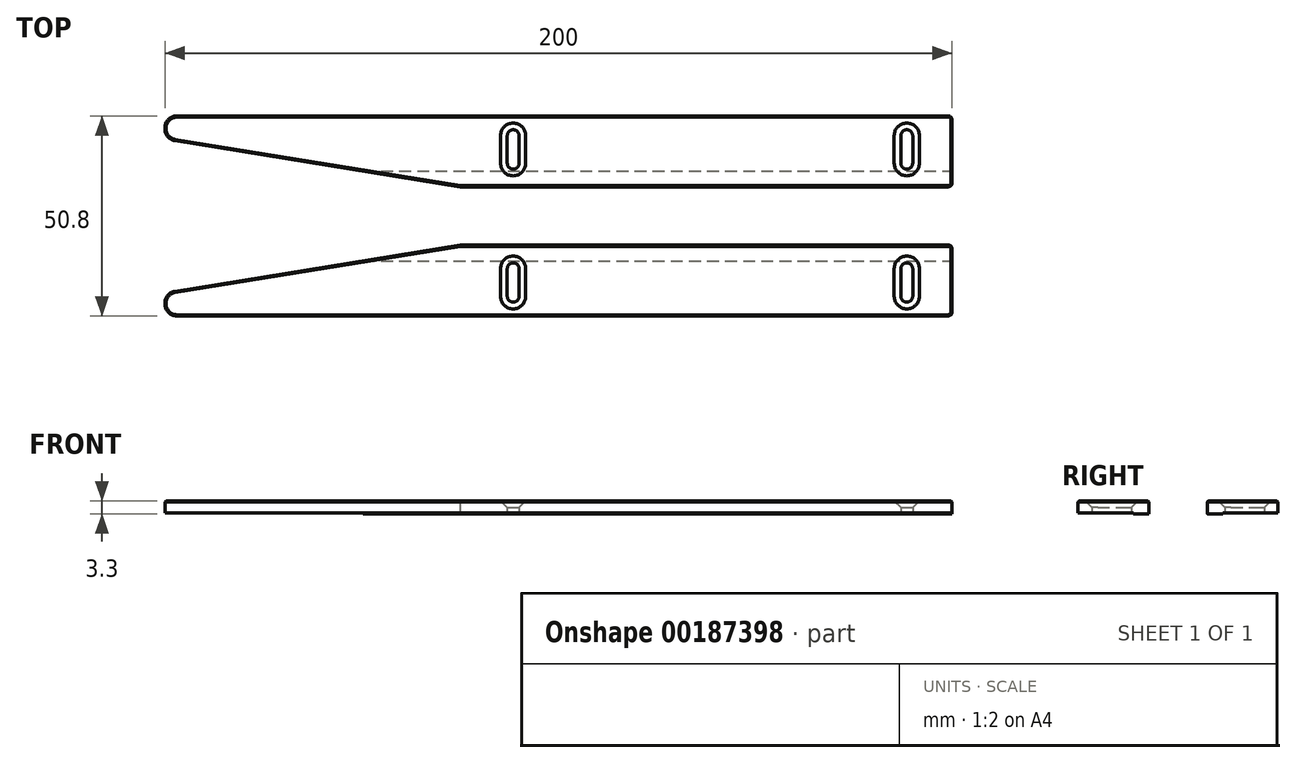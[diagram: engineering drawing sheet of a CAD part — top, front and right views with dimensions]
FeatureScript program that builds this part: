
annotation { "Feature Type Name" : "Feature", "Feature Type Description" : "" }
export const myFeature = defineFeature(function(context is Context, id is Id, definition is map)
    precondition{}
    {
        {
            var Q0;
            Q0=qCreatedBy(makeId("Top.planeOp"),FACE);
            var sketch = newSketch(context, id + "F0", { "sketchPlane" : qUnion([Q0])});
            skLineSegment(sketch, "E0.bottom", {"start": v(0, 0) * mm, "end": v(200, 0) * mm});
            skLineSegment(sketch, "E0.top", {"start": v(0, 18) * mm, "end": v(200, 18) * mm});
            skLineSegment(sketch, "E0.left", {"start": v(0, 0) * mm, "end": v(0, 18) * mm});
            skLineSegment(sketch, "E0.right", {"start": v(200, 0) * mm, "end": v(200, 18) * mm});
            skLineSegment(sketch, "E1.bottom", {"start": v(89.97, 5) * mm, "end": v(86.97, 5) * mm});
            skLineSegment(sketch, "E1.top", {"start": v(89.97, 12) * mm, "end": v(86.97, 12) * mm});
            skLineSegment(sketch, "E1.left", {"start": v(89.97, 5) * mm, "end": v(89.97, 12) * mm});
            skLineSegment(sketch, "E1.right", {"start": v(86.97, 5) * mm, "end": v(86.97, 12) * mm});
            skPoint(sketch, "E1.middle", {"position": v(88.47, 8.5) * mm});
            skLineSegment(sketch, "E2.bottom", {"start": v(189.97, 5) * mm, "end": v(186.97, 5) * mm});
            skLineSegment(sketch, "E2.top", {"start": v(189.97, 12) * mm, "end": v(186.97, 12) * mm});
            skLineSegment(sketch, "E2.left", {"start": v(189.97, 5) * mm, "end": v(189.97, 12) * mm});
            skLineSegment(sketch, "E2.right", {"start": v(186.97, 5) * mm, "end": v(186.97, 12) * mm});
            skPoint(sketch, "E2.middle", {"position": v(188.47, 8.5) * mm});
            skArc(sketch, "E3", {"start": v(86.97, 12) * mm, "mid": v(88.47, 13.5) * mm, "end": v(89.97, 12) * mm});
            skArc(sketch, "E4", {"start": v(186.97, 12) * mm, "mid": v(188.47, 13.5) * mm, "end": v(189.97, 12) * mm});
            skArc(sketch, "E5", {"start": v(86.97, 5) * mm, "mid": v(88.47, 3.5) * mm, "end": v(89.97, 5) * mm});
            skArc(sketch, "E6", {"start": v(186.97, 5) * mm, "mid": v(188.47, 3.5) * mm, "end": v(189.97, 5) * mm});
            skLineSegment(sketch, "E7", {"start": v(0, 5.85) * mm, "end": v(75.04, 18) * mm});
            skSolve(sketch);
        }
        {
            var Q0;
            {var subQ0=sQuery(id+"F0.wireOp",EDGE,"E0.bottom");Q0=makeQuery(id+"F0.imprint","IMPRINT",FACE,{"disambiguationData":[TD([[makeQuery(id+"F0.imprint","IMPRINT",EDGE,{"derivedFrom":subQ0}),1.0]])]});}
            extrude(context, id + "F1", {"entities" : qUnion([Q0]), "depth" : 3 * mm});
        }
        {
            var Q0;
            Q0=makeQuery(id+"F1.opExtrude","CAP_FACE",FACE,{"disambiguationData":[OSD([sQuery(id+"F0.wireOp",EDGE,"E0.bottom"),sQuery(id+"F0.wireOp",EDGE,"E0.top"),sQuery(id+"F0.wireOp",EDGE,"E0.left"),sQuery(id+"F0.wireOp",EDGE,"E0.right"),sQuery(id+"F0.wireOp",EDGE,"E1.left"),sQuery(id+"F0.wireOp",EDGE,"E1.right"),sQuery(id+"F0.wireOp",EDGE,"E2.left"),sQuery(id+"F0.wireOp",EDGE,"E2.right"),sQuery(id+"F0.wireOp",EDGE,"E3"),sQuery(id+"F0.wireOp",EDGE,"E4"),sQuery(id+"F0.wireOp",EDGE,"E5"),sQuery(id+"F0.wireOp",EDGE,"E6"),sQuery(id+"F0.wireOp",EDGE,"E7")])],"isStart":true});
            var sketch = newSketch(context, id + "F2", { "sketchPlane" : qUnion([Q0])});
            skLineSegment(sketch, "E8", {"start": v(75.04, -18) * mm, "end": v(50.33, -14) * mm});
            skLineSegment(sketch, "E9", {"start": v(50.33, -14) * mm, "end": v(200, -14) * mm});
            skLineSegment(sketch, "E10", {"start": v(200, -14) * mm, "end": v(200, -18) * mm});
            skLineSegment(sketch, "E11", {"start": v(200, -18) * mm, "end": v(75.04, -18) * mm});
            skSolve(sketch);
        }
        {
            var Q0;
            {var subQ6=sQuery(id+"F2.wireOp",EDGE,"E8");Q0=makeQuery(id+"F2.imprint","IMPRINT",FACE,{"disambiguationData":[TD([[makeQuery(id+"F2.imprint","IMPRINT",EDGE,{"derivedFrom":subQ6}),1.0]])]});}
            extrude(context, id + "F3", {"entities" : qUnion([Q0]), "operationType" : NewBodyOperationType.ADD, "depth" : .3 * mm});
        }
        {
            var Q0;
            Q0=makeQuery(id+"F1.opExtrude","SWEPT_FACE",FACE,{"disambiguationData":[OSD([sQuery(id+"F0.wireOp",EDGE,"E0.bottom")])]});
            cPlane(context, id + "F4", {"entities" : qUnion([Q0]), "cplaneType" : CPlaneType.OFFSET, "offset" : 25.4 * mm, "oppositeDirection" : true, "width" : 152.4 * mm, "height" : 152.4 * mm});
        }
        {
            var Q0;
            Q0=makeQuery(id+"F1.opExtrude","SWEPT_BODY",BODY,{"disambiguationData":[OSD([sQuery(id+"F0.wireOp",EDGE,"E0.bottom"),sQuery(id+"F0.wireOp",EDGE,"E0.top"),sQuery(id+"F0.wireOp",EDGE,"E0.left"),sQuery(id+"F0.wireOp",EDGE,"E0.right"),sQuery(id+"F0.wireOp",EDGE,"E1.left"),sQuery(id+"F0.wireOp",EDGE,"E1.right"),sQuery(id+"F0.wireOp",EDGE,"E2.left"),sQuery(id+"F0.wireOp",EDGE,"E2.right"),sQuery(id+"F0.wireOp",EDGE,"E3"),sQuery(id+"F0.wireOp",EDGE,"E4"),sQuery(id+"F0.wireOp",EDGE,"E5"),sQuery(id+"F0.wireOp",EDGE,"E6"),sQuery(id+"F0.wireOp",EDGE,"EhPgQ6kI-HOte-GhGe-7i3y-vseyqDZMkckJ")])]});
            var Q1;
            Q1=qCreatedBy(id+"F4.planeOp",FACE);
            mirror(context, id + "F5", {"entities" : qUnion([Q0]), "mirrorPlane" : qUnion([Q1])});
        }
        {
            var Q0;
            Q0=makeQuery(id+"F1.opExtrude","SWEPT_EDGE",EDGE,{"disambiguationData":[OSD([sQuery(id+"F0.wireOp",EDGE,"E0.left"),sQuery(id+"F0.wireOp",EDGE,"EhPgQ6kI-HOte-GhGe-7i3y-vseyqDZMkckJ")])]});
            fillet(context, id + "F6", {"entities" : qUnion([Q0]), "radius" : 3 * mm, "tangentPropagation" : true, "allowEdgeOverflow" : false});
        }
        {
            var Q0;
            Q0=makeQuery(id+"F5.opPattern","COPY",EDGE,{"derivedFrom":makeQuery(id+"F1.opExtrude","SWEPT_EDGE",EDGE,{"disambiguationData":[OSD([sQuery(id+"F0.wireOp",EDGE,"E0.left"),sQuery(id+"F0.wireOp",EDGE,"EhPgQ6kI-HOte-GhGe-7i3y-vseyqDZMkckJ")])]}),"instanceName":"1"});
            fillet(context, id + "F7", {"entities" : qUnion([Q0]), "radius" : 3 * mm, "tangentPropagation" : true, "allowEdgeOverflow" : false});
        }
        {
            var Q0;
            Q0=makeQuery(id+"F1.opExtrude","SWEPT_EDGE",EDGE,{"disambiguationData":[OSD([sQuery(id+"F0.wireOp",EDGE,"E0.bottom"),sQuery(id+"F0.wireOp",EDGE,"E0.right")])]});
            var Q1;
            Q1=makeQuery(id+"F5.opPattern","COPY",EDGE,{"derivedFrom":makeQuery(id+"F1.opExtrude","SWEPT_EDGE",EDGE,{"disambiguationData":[OSD([sQuery(id+"F0.wireOp",EDGE,"E0.bottom"),sQuery(id+"F0.wireOp",EDGE,"E0.right")])]}),"instanceName":"1"});
            var Q2;
            Q2=makeQuery(id+"F1.opExtrude","SWEPT_EDGE",EDGE,{"disambiguationData":[OSD([sQuery(id+"F0.wireOp",EDGE,"E0.top"),sQuery(id+"F0.wireOp",EDGE,"E0.right")])]});
            var Q3;
            Q3=makeQuery(id+"F5.opPattern","COPY",EDGE,{"derivedFrom":makeQuery(id+"F1.opExtrude","SWEPT_EDGE",EDGE,{"disambiguationData":[OSD([sQuery(id+"F0.wireOp",EDGE,"E0.top"),sQuery(id+"F0.wireOp",EDGE,"E0.right")])]}),"instanceName":"1"});
            fillet(context, id + "F8", {"entities" : qUnion([Q0, Q1, Q2, Q3]), "radius" : 1 * mm, "tangentPropagation" : true, "allowEdgeOverflow" : false});
        }
        {
            var Q0;
            Q0=makeQuery(id+"F1.opExtrude","CAP_EDGE",EDGE,{"disambiguationData":[OSD([sQuery(id+"F0.wireOp",EDGE,"E0.top")])],"isStart":false});
            var Q1;
            Q1=makeQuery(id+"F1.opExtrude","CAP_EDGE",EDGE,{"disambiguationData":[OSD([sQuery(id+"F0.wireOp",EDGE,"EhPgQ6kI-HOte-GhGe-7i3y-vseyqDZMkckJ")])],"isStart":false});
            var Q2;
            Q2=makeQuery(id+"F5.opPattern","COPY",EDGE,{"derivedFrom":makeQuery(id+"F1.opExtrude","CAP_EDGE",EDGE,{"disambiguationData":[OSD([sQuery(id+"F0.wireOp",EDGE,"E0.top")])],"isStart":false}),"instanceName":"1"});
            var Q3;
            Q3=makeQuery(id+"F5.opPattern","COPY",EDGE,{"derivedFrom":makeQuery(id+"F1.opExtrude","CAP_EDGE",EDGE,{"disambiguationData":[OSD([sQuery(id+"F0.wireOp",EDGE,"EhPgQ6kI-HOte-GhGe-7i3y-vseyqDZMkckJ")])],"isStart":false}),"instanceName":"1"});
            chamfer(context, id + "F9", {"entities" : qUnion([Q0, Q1, Q2, Q3]), "width" : .3 * mm, "tangentPropagation" : true});
        }
        {
            var Q0;
            Q0=makeQuery(id+"F1.opExtrude","CAP_EDGE",EDGE,{"disambiguationData":[OSD([sQuery(id+"F0.wireOp",EDGE,"E1.left")])],"isStart":false});
            var Q1;
            Q1=makeQuery(id+"F1.opExtrude","CAP_EDGE",EDGE,{"disambiguationData":[OSD([sQuery(id+"F0.wireOp",EDGE,"E3")])],"isStart":false});
            var Q2;
            Q2=makeQuery(id+"F1.opExtrude","CAP_EDGE",EDGE,{"disambiguationData":[OSD([sQuery(id+"F0.wireOp",EDGE,"E1.right")])],"isStart":false});
            var Q3;
            Q3=makeQuery(id+"F1.opExtrude","CAP_EDGE",EDGE,{"disambiguationData":[OSD([sQuery(id+"F0.wireOp",EDGE,"E5")])],"isStart":false});
            var Q4;
            Q4=makeQuery(id+"F1.opExtrude","CAP_EDGE",EDGE,{"disambiguationData":[OSD([sQuery(id+"F0.wireOp",EDGE,"E4")])],"isStart":false});
            var Q5;
            Q5=makeQuery(id+"F1.opExtrude","CAP_EDGE",EDGE,{"disambiguationData":[OSD([sQuery(id+"F0.wireOp",EDGE,"E2.left")])],"isStart":false});
            var Q6;
            Q6=makeQuery(id+"F1.opExtrude","CAP_EDGE",EDGE,{"disambiguationData":[OSD([sQuery(id+"F0.wireOp",EDGE,"E6")])],"isStart":false});
            var Q7;
            Q7=makeQuery(id+"F1.opExtrude","CAP_EDGE",EDGE,{"disambiguationData":[OSD([sQuery(id+"F0.wireOp",EDGE,"E2.right")])],"isStart":false});
            var Q8;
            Q8=makeQuery(id+"F5.opPattern","COPY",EDGE,{"derivedFrom":makeQuery(id+"F1.opExtrude","CAP_EDGE",EDGE,{"disambiguationData":[OSD([sQuery(id+"F0.wireOp",EDGE,"E2.left")])],"isStart":false}),"instanceName":"1"});
            var Q9;
            Q9=makeQuery(id+"F5.opPattern","COPY",EDGE,{"derivedFrom":makeQuery(id+"F1.opExtrude","CAP_EDGE",EDGE,{"disambiguationData":[OSD([sQuery(id+"F0.wireOp",EDGE,"E4")])],"isStart":false}),"instanceName":"1"});
            var Q10;
            Q10=makeQuery(id+"F5.opPattern","COPY",EDGE,{"derivedFrom":makeQuery(id+"F1.opExtrude","CAP_EDGE",EDGE,{"disambiguationData":[OSD([sQuery(id+"F0.wireOp",EDGE,"E2.right")])],"isStart":false}),"instanceName":"1"});
            var Q11;
            Q11=makeQuery(id+"F5.opPattern","COPY",EDGE,{"derivedFrom":makeQuery(id+"F1.opExtrude","CAP_EDGE",EDGE,{"disambiguationData":[OSD([sQuery(id+"F0.wireOp",EDGE,"E6")])],"isStart":false}),"instanceName":"1"});
            var Q12;
            Q12=makeQuery(id+"F5.opPattern","COPY",EDGE,{"derivedFrom":makeQuery(id+"F1.opExtrude","CAP_EDGE",EDGE,{"disambiguationData":[OSD([sQuery(id+"F0.wireOp",EDGE,"E5")])],"isStart":false}),"instanceName":"1"});
            var Q13;
            Q13=makeQuery(id+"F5.opPattern","COPY",EDGE,{"derivedFrom":makeQuery(id+"F1.opExtrude","CAP_EDGE",EDGE,{"disambiguationData":[OSD([sQuery(id+"F0.wireOp",EDGE,"E1.left")])],"isStart":false}),"instanceName":"1"});
            var Q14;
            Q14=makeQuery(id+"F5.opPattern","COPY",EDGE,{"derivedFrom":makeQuery(id+"F1.opExtrude","CAP_EDGE",EDGE,{"disambiguationData":[OSD([sQuery(id+"F0.wireOp",EDGE,"E3")])],"isStart":false}),"instanceName":"1"});
            var Q15;
            Q15=makeQuery(id+"F5.opPattern","COPY",EDGE,{"derivedFrom":makeQuery(id+"F1.opExtrude","CAP_EDGE",EDGE,{"disambiguationData":[OSD([sQuery(id+"F0.wireOp",EDGE,"E1.right")])],"isStart":false}),"instanceName":"1"});
            chamfer(context, id + "F10", {"entities" : qUnion([Q0, Q1, Q2, Q3, Q4, Q5, Q6, Q7, Q8, Q9, Q10, Q11, Q12, Q13, Q14, Q15]), "chamferType" : ChamferType.OFFSET_ANGLE, "width" : 1.7 * mm, "oppositeDirection" : false, "angle" : 45 * degree, "tangentPropagation" : true});
        }
    });
